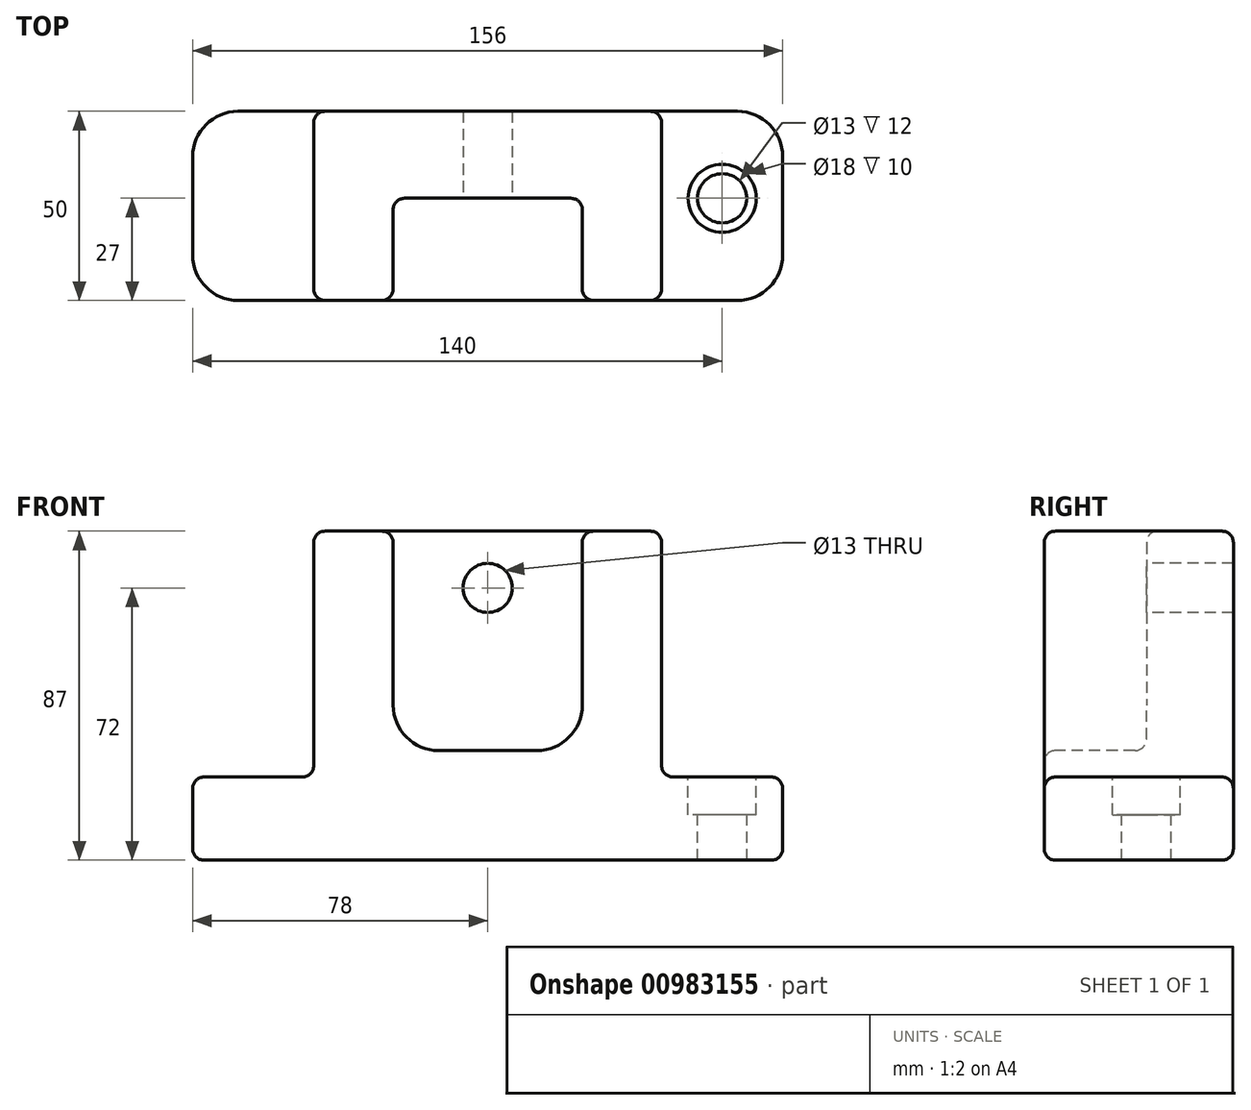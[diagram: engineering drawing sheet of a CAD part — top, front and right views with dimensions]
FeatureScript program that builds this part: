
annotation { "Feature Type Name" : "Feature", "Feature Type Description" : "" }
export const myFeature = defineFeature(function(context is Context, id is Id, definition is map)
    precondition{}
    {
        {
            var Q0;
            Q0=qCreatedBy(makeId("Front.planeOp"),FACE);
            var sketch = newSketch(context, id + "F0", { "sketchPlane" : qUnion([Q0])});
            skLineSegment(sketch, "E0", {"start": v(0, 0) * mm, "end": v(0, 87) * mm, "construction": true});
            skLineSegment(sketch, "E1", {"start": v(0, 87) * mm, "end": v(46, 87) * mm});
            skLineSegment(sketch, "E2", {"start": v(46, 87) * mm, "end": v(46, 22) * mm});
            skLineSegment(sketch, "E3", {"start": v(46, 22) * mm, "end": v(78, 22) * mm});
            skLineSegment(sketch, "E4", {"start": v(78, 22) * mm, "end": v(78, 0) * mm});
            skLineSegment(sketch, "E5", {"start": v(78, 0) * mm, "end": v(0, 0) * mm});
            skLineSegment(sketch, "E6.MirrorCS", {"start": v(-46, 87) * mm, "end": v(-46, 22) * mm});
            skLineSegment(sketch, "E7.MirrorCS", {"start": v(-46, 22) * mm, "end": v(-78, 22) * mm});
            skLineSegment(sketch, "E8.MirrorCS", {"start": v(-78, 22) * mm, "end": v(-78, 0) * mm});
            skLineSegment(sketch, "E9.MirrorCS", {"start": v(0, 87) * mm, "end": v(-46, 87) * mm});
            skLineSegment(sketch, "E10.MirrorCS", {"start": v(-78, 0) * mm, "end": v(0, 0) * mm});
            skSolve(sketch);
        }
        {
            var Q0;
            Q0 = qSketchRegion(id + "F0", true);
            extrude(context, id + "F1", {"entities" : qUnion([Q0]), "endBound" : BoundingType.SYMMETRIC, "depth" : 50 * mm, "offsetDistance" : 25 * mm});
        }
        {
            var Q0;
            Q0=makeQuery(id+"F1.opExtrude","CAP_FACE",FACE,{"disambiguationData":[OSD([sQuery(id+"F0.wireOp",EDGE,"E1"),sQuery(id+"F0.wireOp",EDGE,"E2"),sQuery(id+"F0.wireOp",EDGE,"E3"),sQuery(id+"F0.wireOp",EDGE,"E4"),sQuery(id+"F0.wireOp",EDGE,"E5"),sQuery(id+"F0.wireOp",EDGE,"E6.MirrorCS"),sQuery(id+"F0.wireOp",EDGE,"E7.MirrorCS"),sQuery(id+"F0.wireOp",EDGE,"E8.MirrorCS"),sQuery(id+"F0.wireOp",EDGE,"E9.MirrorCS"),sQuery(id+"F0.wireOp",EDGE,"E10.MirrorCS")])],"isStart":false});
            var sketch = newSketch(context, id + "F2", { "sketchPlane" : qUnion([Q0])});
            skLineSegment(sketch, "E11", {"start": v(0, 29) * mm, "end": v(0, 87) * mm, "construction": true});
            skLineSegment(sketch, "E12", {"start": v(0, 87) * mm, "end": v(25, 87) * mm});
            skLineSegment(sketch, "E13", {"start": v(25, 87) * mm, "end": v(25, 29) * mm});
            skLineSegment(sketch, "E14", {"start": v(25, 29) * mm, "end": v(0, 29) * mm});
            skLineSegment(sketch, "E15.MirrorCS", {"start": v(-25, 87) * mm, "end": v(-25, 29) * mm});
            skLineSegment(sketch, "E16.MirrorCS", {"start": v(-25, 29) * mm, "end": v(0, 29) * mm});
            skLineSegment(sketch, "E17.MirrorCS", {"start": v(0, 87) * mm, "end": v(-25, 87) * mm});
            skSolve(sketch);
        }
        {
            var Q0;
            Q0 = qSketchRegion(id + "F2", true);
            extrude(context, id + "F3", {"entities" : qUnion([Q0]), "operationType" : NewBodyOperationType.REMOVE, "oppositeDirection" : true, "depth" : 27 * mm, "offsetDistance" : 25 * mm});
        }
        {
            var Q0;
            Q0=makeQuery(id+"F3.boolean.opBoolean","COPY",FACE,{"derivedFrom":makeQuery(id+"F3.opExtrude","CAP_FACE",FACE,{"disambiguationData":[OSD([sQuery(id+"F2.wireOp",EDGE,"E12"),sQuery(id+"F2.wireOp",EDGE,"E13"),sQuery(id+"F2.wireOp",EDGE,"E14"),sQuery(id+"F2.wireOp",EDGE,"E15.MirrorCS"),sQuery(id+"F2.wireOp",EDGE,"E16.MirrorCS"),sQuery(id+"F2.wireOp",EDGE,"E17.MirrorCS")])],"isStart":false})});
            var sketch = newSketch(context, id + "F4", { "sketchPlane" : qUnion([Q0])});
            skCircle(sketch, "E18", {"center": v(0, 72) * mm, "radius": 6.5 * mm});
            skSolve(sketch);
        }
        {
            var Q0;
            Q0 = qSketchRegion(id + "F4", true);
            extrude(context, id + "F5", {"entities" : qUnion([Q0]), "operationType" : NewBodyOperationType.REMOVE, "oppositeDirection" : true, "depth" : 25 * mm, "offsetDistance" : 25 * mm});
        }
        {
            var Q0;
            Q0=makeQuery(id+"F1.opExtrude","SWEPT_FACE",FACE,{"disambiguationData":[OSD([sQuery(id+"F0.wireOp",EDGE,"E3")])]});
            var sketch = newSketch(context, id + "F6", { "sketchPlane" : qUnion([Q0])});
            skCircle(sketch, "E19", {"center": v(62, 2) * mm, "radius": 6.5 * mm});
            skSolve(sketch);
        }
        {
            var Q0;
            Q0 = qSketchRegion(id + "F6", true);
            extrude(context, id + "F7", {"entities" : qUnion([Q0]), "operationType" : NewBodyOperationType.REMOVE, "endBound" : BoundingType.THROUGH_ALL, "oppositeDirection" : true, "depth" : 25 * mm, "offsetDistance" : 25 * mm});
        }
        {
            var Q0;
            Q0=makeQuery(id+"F1.opExtrude","SWEPT_FACE",FACE,{"disambiguationData":[OSD([sQuery(id+"F0.wireOp",EDGE,"E3")])]});
            var sketch = newSketch(context, id + "F8", { "sketchPlane" : qUnion([Q0])});
            skCircle(sketch, "E20", {"center": v(62, 2) * mm, "radius": 9 * mm});
            skSolve(sketch);
        }
        {
            var Q0;
            Q0=makeQuery(id+"F8.imprint","IMPRINT",FACE,{"disambiguationData":[TD([[makeQuery(id+"F8.imprint","IMPRINT",EDGE,{"derivedFrom":sQuery(id+"F8.wireOp",EDGE,"E20")}),1.0]])]});
            extrude(context, id + "F9", {"entities" : qUnion([Q0]), "operationType" : NewBodyOperationType.REMOVE, "oppositeDirection" : true, "depth" : 10 * mm, "offsetDistance" : 25 * mm});
        }
        {
            var Q0;
            Q0=makeQuery(id+"F3.boolean.opBoolean","COPY",EDGE,{"derivedFrom":makeQuery(id+"F3.opExtrude","SWEPT_EDGE",EDGE,{"disambiguationData":[OSD([sQuery(id+"F2.wireOp",EDGE,"E15.MirrorCS"),sQuery(id+"F2.wireOp",EDGE,"E16.MirrorCS")])]})});
            var Q1;
            Q1=makeQuery(id+"F3.boolean.opBoolean","COPY",EDGE,{"derivedFrom":makeQuery(id+"F3.opExtrude","SWEPT_EDGE",EDGE,{"disambiguationData":[OSD([sQuery(id+"F2.wireOp",EDGE,"E13"),sQuery(id+"F2.wireOp",EDGE,"E14")])]})});
            var Q2;
            Q2=makeQuery(id+"F1.opExtrude","CAP_EDGE",EDGE,{"disambiguationData":[OSD([sQuery(id+"F0.wireOp",EDGE,"E4")])],"isStart":false});
            var Q3;
            Q3=makeQuery(id+"F1.opExtrude","CAP_EDGE",EDGE,{"disambiguationData":[OSD([sQuery(id+"F0.wireOp",EDGE,"E8.MirrorCS")])],"isStart":false});
            var Q4;
            Q4=makeQuery(id+"F1.opExtrude","CAP_EDGE",EDGE,{"disambiguationData":[OSD([sQuery(id+"F0.wireOp",EDGE,"E8.MirrorCS")])],"isStart":true});
            var Q5;
            Q5=makeQuery(id+"F1.opExtrude","CAP_EDGE",EDGE,{"disambiguationData":[OSD([sQuery(id+"F0.wireOp",EDGE,"E4")])],"isStart":true});
            fillet(context, id + "F10", {"entities" : qUnion([Q0, Q1, Q2, Q3, Q4, Q5]), "radius" : 12 * mm, "tangentPropagation" : true, "allowEdgeOverflow" : false});
        }
        {
            var Q0;
            Q0=makeQuery(id+"F1.opExtrude","SWEPT_FACE",FACE,{"disambiguationData":[OSD([sQuery(id+"F0.wireOp",EDGE,"E1"),sQuery(id+"F0.wireOp",EDGE,"E9.MirrorCS")])]});
            var Q1;
            Q1=makeQuery(id+"F1.opExtrude","CAP_FACE",FACE,{"disambiguationData":[OSD([sQuery(id+"F0.wireOp",EDGE,"E1"),sQuery(id+"F0.wireOp",EDGE,"E2"),sQuery(id+"F0.wireOp",EDGE,"E3"),sQuery(id+"F0.wireOp",EDGE,"E4"),sQuery(id+"F0.wireOp",EDGE,"E5"),sQuery(id+"F0.wireOp",EDGE,"E6.MirrorCS"),sQuery(id+"F0.wireOp",EDGE,"E7.MirrorCS"),sQuery(id+"F0.wireOp",EDGE,"E8.MirrorCS"),sQuery(id+"F0.wireOp",EDGE,"E9.MirrorCS"),sQuery(id+"F0.wireOp",EDGE,"E10.MirrorCS")])],"isStart":false});
            var Q2;
            Q2=makeQuery(id+"F1.opExtrude","SWEPT_FACE",FACE,{"disambiguationData":[OSD([sQuery(id+"F0.wireOp",EDGE,"E2")])]});
            var Q3;
            Q3=makeQuery(id+"F1.opExtrude","SWEPT_FACE",FACE,{"disambiguationData":[OSD([sQuery(id+"F0.wireOp",EDGE,"E6.MirrorCS")])]});
            var Q4;
            Q4=makeQuery(id+"F3.boolean.opBoolean","COPY",EDGE,{"derivedFrom":makeQuery(id+"F3.opExtrude","CAP_EDGE",EDGE,{"disambiguationData":[OSD([sQuery(id+"F2.wireOp",EDGE,"E15.MirrorCS")])],"isStart":false})});
            fillet(context, id + "F11", {"entities" : qUnion([Q0, Q1, Q2, Q3, Q4]), "radius" : 3 * mm, "tangentPropagation" : true, "allowEdgeOverflow" : false});
        }
    });
